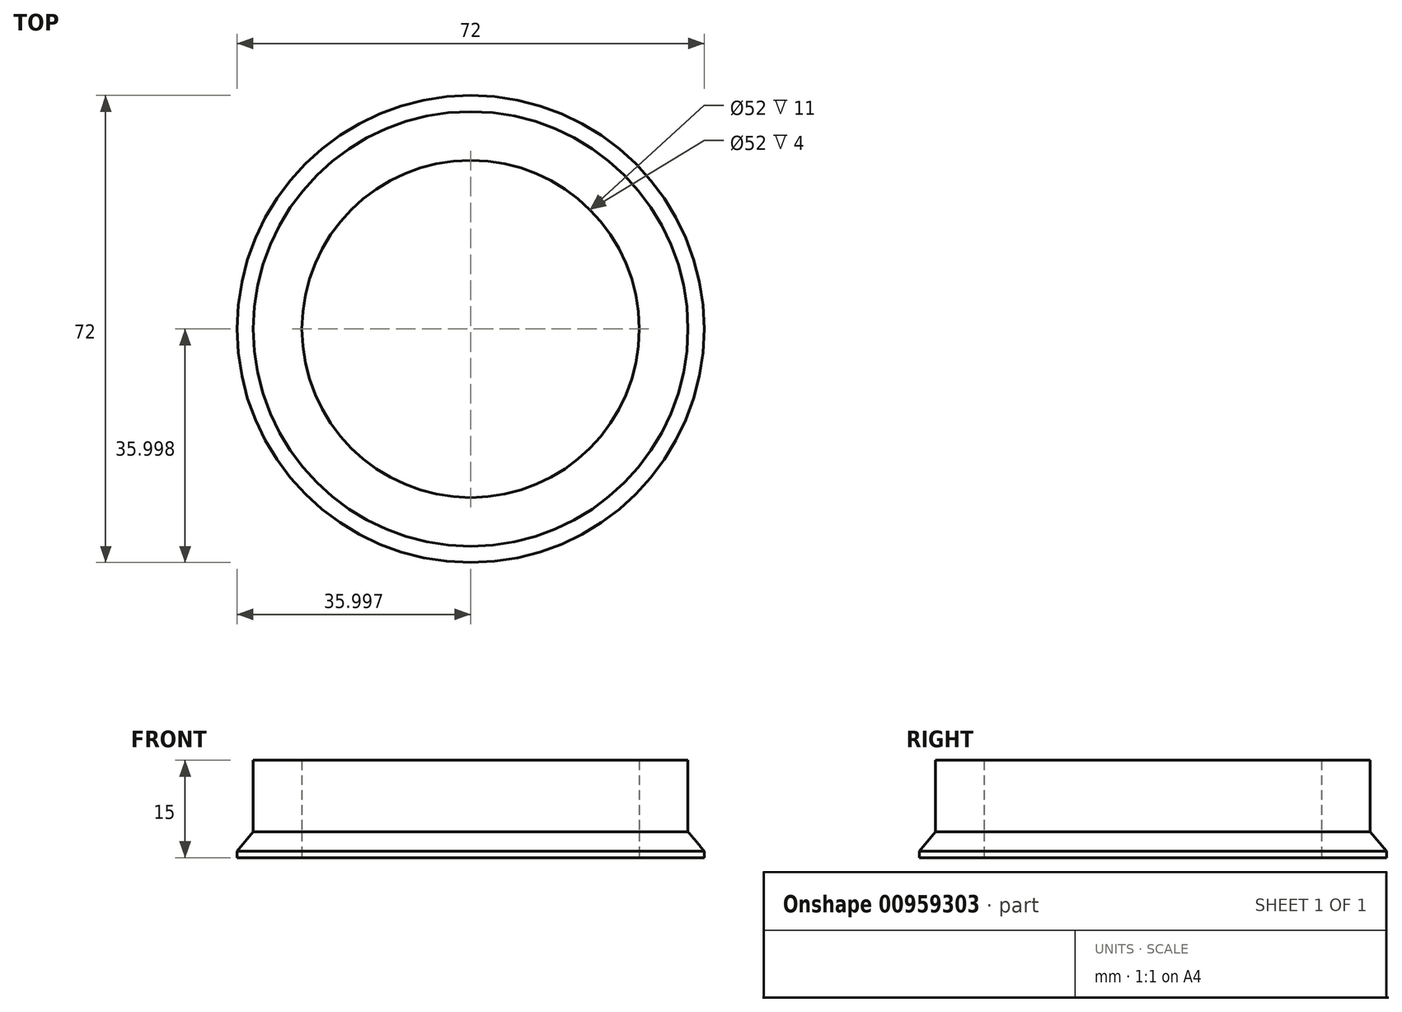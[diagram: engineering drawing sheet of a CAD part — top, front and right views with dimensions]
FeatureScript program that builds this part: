
annotation { "Feature Type Name" : "Feature", "Feature Type Description" : "" }
export const myFeature = defineFeature(function(context is Context, id is Id, definition is map)
    precondition{}
    {
        {
            var Q0;
            Q0=qCreatedBy(makeId("Top.planeOp"),FACE);
            var sketch = newSketch(context, id + "F0", { "sketchPlane" : qUnion([Q0])});
            skCircle(sketch, "E0", {"center": v(-21.94, 7.57) * mm, "radius": 36 * mm});
            skCircle(sketch, "E1", {"center": v(-21.94, 7.57) * mm, "radius": 26 * mm});
            skSolve(sketch);
        }
        {
            var Q0;
            Q0 = qSketchRegion(id + "F0", true);
            extrude(context, id + "F1", {"entities" : qUnion([Q0]), "depth" : 4 * mm, "offsetDistance" : 25 * mm});
        }
        {
            var Q0;
            Q0=makeQuery(id+"F1.opExtrude","CAP_FACE",FACE,{"disambiguationData":[OSD([sQuery(id+"F0.wireOp",EDGE,"E0"),sQuery(id+"F0.wireOp",EDGE,"E1")])],"isStart":false});
            var sketch = newSketch(context, id + "F2", { "sketchPlane" : qUnion([Q0])});
            skCircle(sketch, "E2", {"center": v(-21.94, 7.57) * mm, "radius": 33.5 * mm});
            skSolve(sketch);
        }
        {
            var Q0;
            Q0=makeQuery(id+"F2.imprint","IMPRINT",FACE,{"disambiguationData":[TD([[makeQuery(id+"F2.imprint","IMPRINT",EDGE,{"derivedFrom":sQuery(id+"F2.wireOp",EDGE,"E2")}),1.0]])]});
            extrude(context, id + "F3", {"entities" : qUnion([Q0]), "depth" : 11 * mm, "offsetDistance" : 25 * mm});
        }
        {
            var Q0;
            Q0=makeQuery(id+"F1.opExtrude","CAP_EDGE",EDGE,{"disambiguationData":[OSD([sQuery(id+"F0.wireOp",EDGE,"E0")])],"isStart":false});
            chamfer(context, id + "F4", {"entities" : qUnion([Q0]), "chamferType" : ChamferType.TWO_OFFSETS, "width1" : 2.5 * mm, "oppositeDirection" : false, "width2" : 3 * mm, "tangentPropagation" : true});
        }
    });
